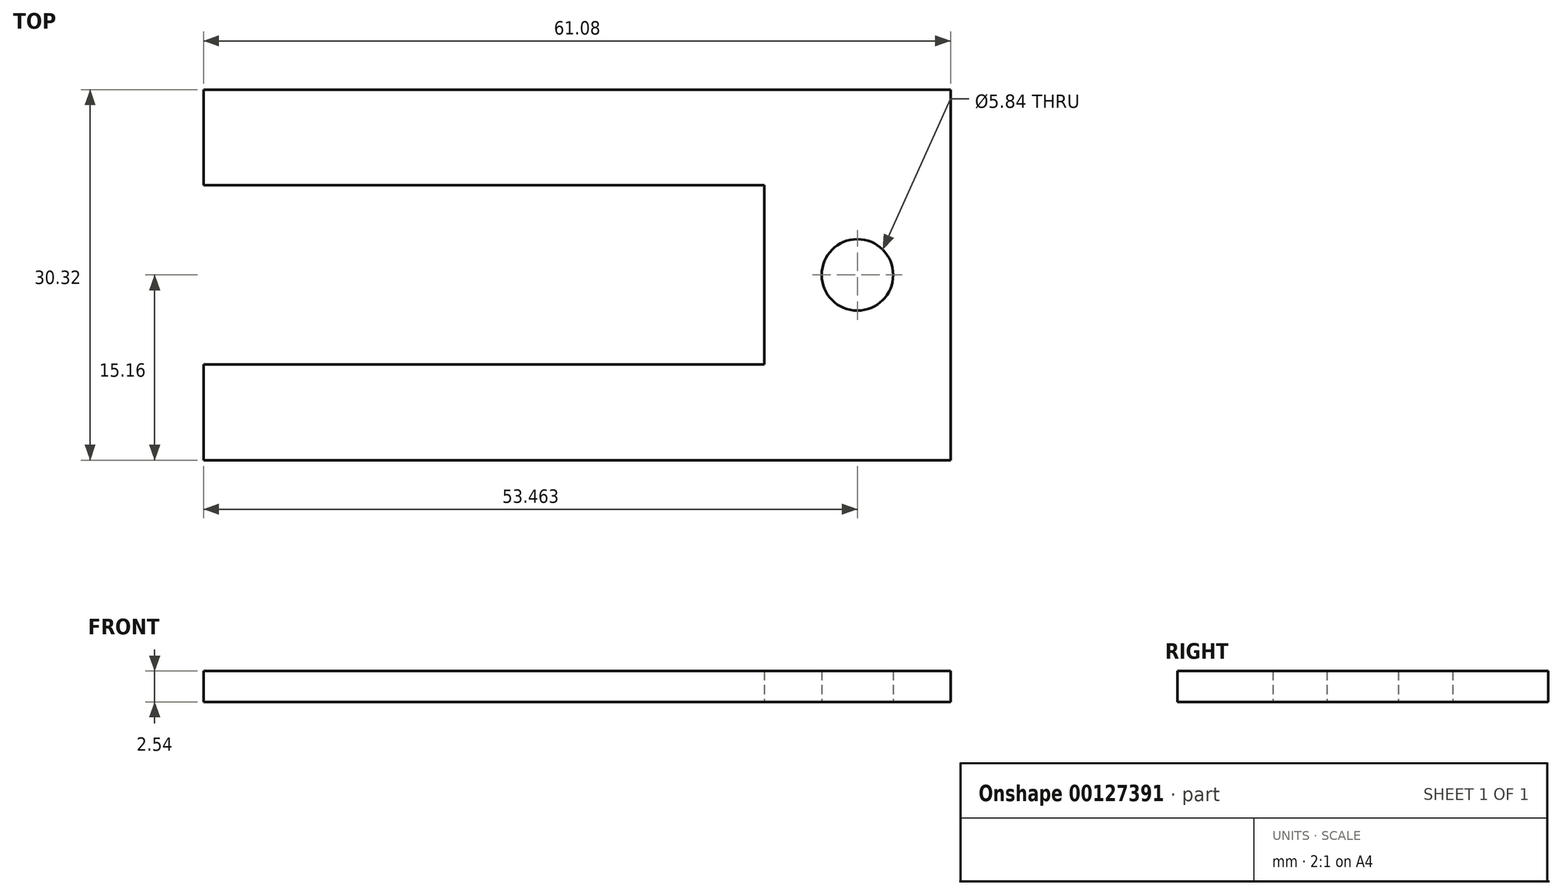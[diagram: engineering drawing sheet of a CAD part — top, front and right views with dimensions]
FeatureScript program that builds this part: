
annotation { "Feature Type Name" : "Feature", "Feature Type Description" : "" }
export const myFeature = defineFeature(function(context is Context, id is Id, definition is map)
    precondition{}
    {
        {
            var Q0;
            Q0=qCreatedBy(makeId("Top.planeOp"),FACE);
            var sketch = newSketch(context, id + "F0", { "sketchPlane" : qUnion([Q0])});
            skLineSegment(sketch, "E0.bottom", {"start": v(30.54, 15.16) * mm, "end": v(-30.54, 15.16) * mm});
            skLineSegment(sketch, "E0.top", {"start": v(30.54, -15.16) * mm, "end": v(-30.54, -15.16) * mm});
            skLineSegment(sketch, "E0.left", {"start": v(30.54, 15.16) * mm, "end": v(30.54, -15.16) * mm});
            skLineSegment(sketch, "E0.right", {"start": v(-30.54, 15.16) * mm, "end": v(-30.54, -15.16) * mm});
            skPoint(sketch, "E0.middle", {"position": v(0, 0) * mm});
            skLineSegment(sketch, "E1.bottom", {"start": v(-30.54, 7.34) * mm, "end": v(15.3, 7.34) * mm});
            skLineSegment(sketch, "E1.top", {"start": v(-30.54, -7.34) * mm, "end": v(15.3, -7.34) * mm});
            skLineSegment(sketch, "E1.right", {"start": v(15.3, 7.34) * mm, "end": v(15.3, -7.34) * mm});
            skCircle(sketch, "E2", {"center": v(22.92, 0) * mm, "radius": 2.92 * mm});
            skSolve(sketch);
        }
        {
            var Q0;
            {var subQ1=sQuery(id+"F0.wireOp",EDGE,"E0.bottom");Q0=makeQuery(id+"F0.imprint","IMPRINT",FACE,{"disambiguationData":[TD([[makeQuery(id+"F0.imprint","IMPRINT",EDGE,{"derivedFrom":subQ1}),1.0]])]});}
            extrude(context, id + "F1", {"entities" : qUnion([Q0]), "endBound" : BoundingType.SYMMETRIC, "depth" : 2.54 * mm});
        }
    });
